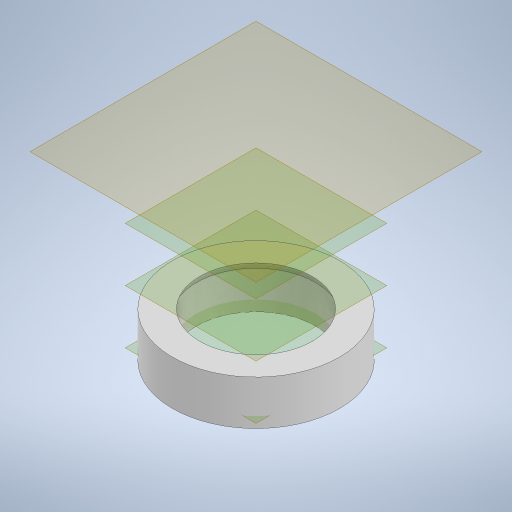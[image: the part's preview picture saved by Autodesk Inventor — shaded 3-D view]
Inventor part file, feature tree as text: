
AUTODESK INVENTOR PART (.ipt)
format: ipt  version: 2024 (Build 280153020, 153B)  size: 329,728 bytes
history: native  units: in
note: dims shown in document units (in); Inventor stores cm internally (conversion verified against a paired STEP export)
features: sketch x8, extrude x4, plane x4, loft x1, mirror x1
ambient origin geometry x8: Origin, YZ Plane, XZ Plane, XY Plane, X Axis, Y Axis, Z Axis, Center Point
bodies: Solid1 (feature_tree)
feature tree (18):
  extrude  "Extrusion1"  Depth=2.6378in TaperAngle=0.0deg
  extrude  "Extrusion2"  Depth=0.2756in TaperAngle=0.0deg
  plane  "Work Plane1"
  plane  "Work Plane2"
  sketch  "Sketch4"  dims[d6=-0.5906in d7=1.1in]
  sketch  "Sketch5"  dims[d8=0.1969in d10=-0.1969in]
  plane  "Work Plane3"
  plane  "Work Plane4"
  loft  "Loft1"
  mirror  "Mirror1"
  extrude  "Extrusion3"  [1 undecoded]
  extrude  "Extrusion4"  Depth=1.1in
  sketch  "Sketch1"  dims[d0=1.5in d1=2.6378in d2=0.0in]
  sketch  "Sketch2"  dims[d3=0.8681in d4=0.2756in d5=0.0in]
  sketch  "Sketch8"  dims[d11=0.748in d12=1.1in]
  sketch  "Sketch9"  dims[d13=0.0in d14=90.0deg]
  sketch  "Sketch10"  dims[d15=0.0in d16=90.0deg]
  sketch  "Sketch11"  dims[d17=0.0in d18=90.0deg d19=0.0in d20=90.0deg d21=2.3125in d22=0.0in d23=2.3125in d24=0.0in]
note: 1 required parameter value undecoded (feature->parameter linkage not recoverable at this tier; creation-order binding heuristic only, values carry confidence <= 0.55)
